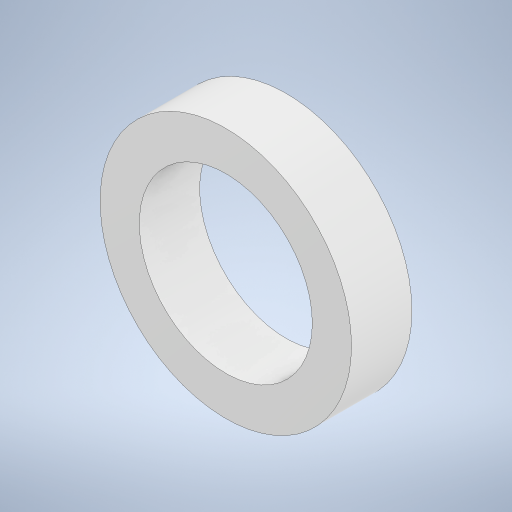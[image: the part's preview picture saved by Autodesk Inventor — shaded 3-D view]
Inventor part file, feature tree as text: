
AUTODESK INVENTOR PART (.ipt)
format: ipt  version: 2024 (Build 280153000, 153)  size: 230,912 bytes
history: native  units: mm
features: extrude x1, sketch x1
ambient origin geometry x8: Origin, YZ Plane, XZ Plane, XY Plane, X Axis, Y Axis, Z Axis, Center Point
bodies: Solid1 (feature_tree)
feature tree (2):
  extrude  "Extrusion1"  Depth=1.85mm
  sketch  "Sketch1"  dims[d0=5.3mm d1=1.2mm d2=1.85mm d3=0.0mm]
